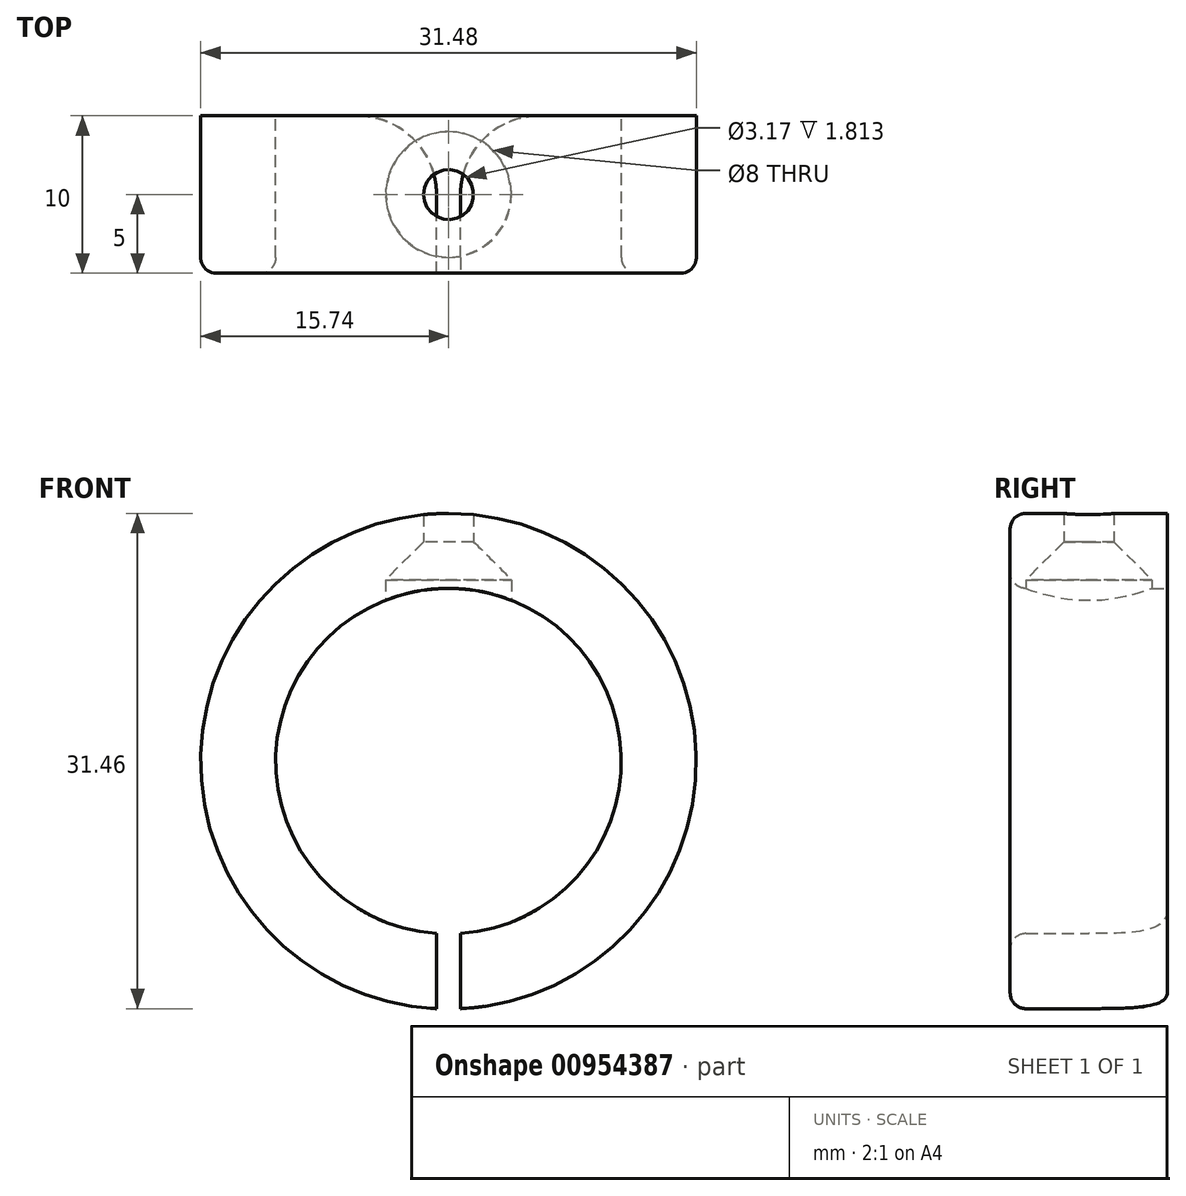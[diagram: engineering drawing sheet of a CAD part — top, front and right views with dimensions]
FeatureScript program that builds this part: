
annotation { "Feature Type Name" : "Feature", "Feature Type Description" : "" }
export const myFeature = defineFeature(function(context is Context, id is Id, definition is map)
    precondition{}
    {
        {
            var Q0;
            Q0=qCreatedBy(makeId("Front.planeOp"),FACE);
            var sketch = newSketch(context, id + "F0", { "sketchPlane" : qUnion([Q0])});
            skCircle(sketch, "E0", {"center": v(0, 0) * mm, "radius": 10.97 * mm});
            skCircle(sketch, "E1", {"center": v(0, 0) * mm, "radius": 15.74 * mm});
            skSolve(sketch);
        }
        {
            var Q0;
            Q0 = qSketchRegion(id + "F0", true);
            extrude(context, id + "F1", {"entities" : qUnion([Q0]), "depth" : 10 * mm, "offsetDistance" : 25 * mm});
        }
        {
            var Q0;
            Q0=makeQuery(id+"F1.opExtrude","CAP_FACE",FACE,{"disambiguationData":[OSD([sQuery(id+"F0.wireOp",EDGE,"E0"),sQuery(id+"F0.wireOp",EDGE,"E1")])],"isStart":false});
            var sketch = newSketch(context, id + "F2", { "sketchPlane" : qUnion([Q0])});
            skLineSegment(sketch, "E2.bottom", {"start": v(-0.76, -7.67) * mm, "end": v(0.76, -7.67) * mm});
            skLineSegment(sketch, "E2.top", {"start": v(-0.76, -15.74) * mm, "end": v(0.76, -15.74) * mm});
            skLineSegment(sketch, "E2.left", {"start": v(-0.76, -7.67) * mm, "end": v(-0.76, -15.74) * mm});
            skLineSegment(sketch, "E2.right", {"start": v(0.76, -7.67) * mm, "end": v(0.76, -15.74) * mm});
            skSolve(sketch);
        }
        {
            var Q0;
            Q0 = qSketchRegion(id + "F2", true);
            extrude(context, id + "F3", {"entities" : qUnion([Q0]), "operationType" : NewBodyOperationType.REMOVE, "oppositeDirection" : true, "depth" : 25 * mm, "offsetDistance" : 25 * mm});
        }
        {
            var Q0;
            Q0=makeQuery(id+"F3.boolean.opBoolean","COPY",EDGE,{"derivedFrom":makeQuery(id+"F3.opExtrude","CAP_EDGE",EDGE,{"disambiguationData":[OSD([sQuery(id+"F2.wireOp",EDGE,"E2.left")])],"isStart":true})});
            var Q1;
            Q1=makeQuery(id+"F3.boolean.opBoolean","INTERSECT",EDGE,{"derivedFrom":[makeQuery(id+"F1.opExtrude","CAP_FACE",FACE,{"disambiguationData":[OSD([sQuery(id+"F0.wireOp",EDGE,"E0"),sQuery(id+"F0.wireOp",EDGE,"E1")])],"isStart":true}),makeQuery(id+"F3.opExtrude","SWEPT_FACE",FACE,{"disambiguationData":[OSD([sQuery(id+"F2.wireOp",EDGE,"E2.left")])]})]});
            var Q2;
            Q2=makeQuery(id+"F3.boolean.opBoolean","COPY",EDGE,{"derivedFrom":makeQuery(id+"F3.opExtrude","CAP_EDGE",EDGE,{"disambiguationData":[OSD([sQuery(id+"F2.wireOp",EDGE,"E2.right")])],"isStart":true})});
            var Q3;
            Q3=makeQuery(id+"F3.boolean.opBoolean","INTERSECT",EDGE,{"derivedFrom":[makeQuery(id+"F1.opExtrude","CAP_FACE",FACE,{"disambiguationData":[OSD([sQuery(id+"F0.wireOp",EDGE,"E0"),sQuery(id+"F0.wireOp",EDGE,"E1")])],"isStart":true}),makeQuery(id+"F3.opExtrude","SWEPT_FACE",FACE,{"disambiguationData":[OSD([sQuery(id+"F2.wireOp",EDGE,"E2.right")])]})]});
            fillet(context, id + "F4", {"entities" : qUnion([Q0, Q1, Q2, Q3]), "radius" : 5 * mm, "tangentPropagation" : true, "allowEdgeOverflow" : false});
        }
        {
            var Q0;
            Q0=qCreatedBy(makeId("Top.planeOp"),FACE);
            var sketch = newSketch(context, id + "F5", { "sketchPlane" : qUnion([Q0])});
            skCircle(sketch, "E3", {"center": v(0, -5) * mm, "radius": 1.59 * mm});
            skSolve(sketch);
        }
        {
            var Q0;
            Q0 = qSketchRegion(id + "F5", true);
            extrude(context, id + "F6", {"entities" : qUnion([Q0]), "operationType" : NewBodyOperationType.REMOVE, "depth" : 25 * mm, "offsetDistance" : 25 * mm});
        }
        {
            var Q0;
            Q0=qCreatedBy(makeId("Front.planeOp"),FACE);
            var sketch = newSketch(context, id + "F7", { "sketchPlane" : qUnion([Q0])});
            skCircle(sketch, "E4", {"center": v(0, 0) * mm, "radius": 13.5 * mm});
            skSolve(sketch);
        }
        {
            var Q0;
            Q0 = qSketchRegion(id + "F7", true);
            var Q1;
            Q1=sQuery(id+"F7.wireOp",EDGE,"E4");
            extrude(context, id + "F8", {"entities" : qUnion([Q0]), "bodyType" : ToolBodyType.SURFACE, "surfaceEntities" : qUnion([Q1]), "endBound" : BoundingType.UP_TO_NEXT, "depth" : 25 * mm, "offsetDistance" : 25 * mm});
        }
        {
            var Q0;
            Q0=makeQuery(id+"F1.opExtrude","CAP_EDGE",EDGE,{"disambiguationData":[OSD([sQuery(id+"F0.wireOp",EDGE,"E0")])],"isStart":false});
            var Q1;
            Q1=makeQuery(id+"F1.opExtrude","CAP_EDGE",EDGE,{"disambiguationData":[OSD([sQuery(id+"F0.wireOp",EDGE,"E1")])],"isStart":false});
            fillet(context, id + "F9", {"entities" : qUnion([Q0, Q1]), "radius" : 1 * mm, "tangentPropagation" : true, "allowEdgeOverflow" : false});
        }
        {
            var Q0;
            Q0=qCreatedBy(makeId("Top.planeOp"),FACE);
            var sketch = newSketch(context, id + "F10", { "sketchPlane" : qUnion([Q0])});
            skCircle(sketch, "E5", {"center": v(0, -5) * mm, "radius": 4 * mm});
            skSolve(sketch);
        }
        {
            var Q0;
            Q0=makeQuery(id+"F10.imprint","IMPRINT",FACE,{"disambiguationData":[TD([[makeQuery(id+"F10.imprint","IMPRINT",EDGE,{"derivedFrom":sQuery(id+"F10.wireOp",EDGE,"E5")}),1.0]])]});
            var Q1;
            Q1=makeQuery(id+"F8.opExtrude","SWEPT_BODY",BODY,{"disambiguationData":[OSD([sQuery(id+"F7.wireOp",EDGE,"E4")])]});
            extrude(context, id + "F11", {"entities" : qUnion([Q0]), "operationType" : NewBodyOperationType.REMOVE, "depth" : 13.93 * mm, "endBoundEntityBody" : qUnion([Q1]), "offsetDistance" : 25 * mm});
        }
        {
            var Q0;
            Q0=makeQuery(id+"F11.boolean.opBoolean","COPY",EDGE,{"derivedFrom":makeQuery(id+"F11.opExtrude","CAP_EDGE",EDGE,{"disambiguationData":[OSD([sQuery(id+"F10.wireOp",EDGE,"E5")])],"isStart":false})});
            chamfer(context, id + "F12", {"entities" : qUnion([Q0]), "width" : 2.4 * mm, "tangentPropagation" : true});
        }
    });
